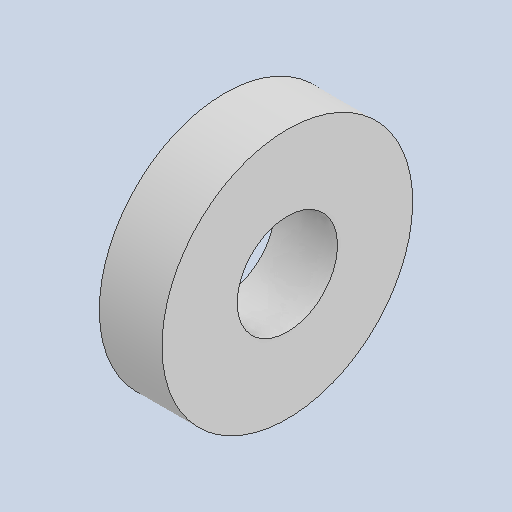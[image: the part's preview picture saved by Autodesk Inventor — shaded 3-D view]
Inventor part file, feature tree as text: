
AUTODESK INVENTOR PART (.ipt)
format: ipt  version: 2024 (Build 280153000, 153)  size: 96,768 bytes
history: native  units: in
note: dims shown in document units (in); Inventor stores cm internally (conversion verified against a paired STEP export)
features: extrude x1, sketch x1
ambient origin geometry x8: Origin, YZ Plane, XZ Plane, XY Plane, X Axis, Y Axis, Z Axis, Center Point
bodies: Solid1 (feature_tree)
feature tree (2):
  extrude  "Extrusion1"  Depth=0.125in
  sketch  "Sketch1"  dims[d0=0.2in d1=0.15in d2=0.125in d3=0.0in]
